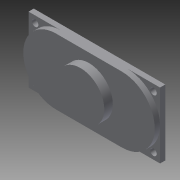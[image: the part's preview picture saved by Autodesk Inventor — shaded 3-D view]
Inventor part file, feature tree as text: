
AUTODESK INVENTOR PART (.ipt)
format: ipt  version: 2016 (Build 200138000, 138)  size: 116,736 bytes
history: native  units: mm
features: sketch x4, extrude x3, hole x1
ambient origin geometry x8: Origin, YZ Plane, XZ Plane, XY Plane, X Axis, Y Axis, Z Axis, Center Point
bodies: Solid1 (feature_tree)
feature tree (8):
  extrude  "Extrusion1"  Depth=20.0mm
  extrude  "Extrusion2"  Depth=20.0mm
  extrude  "Extrusion3"  Depth=10.0mm
  hole  "Hole1"  [1 undecoded]
  sketch  "Sketch1"  dims[d0=40.0mm d1=20.0mm]
  sketch  "Sketch2"  dims[d2=10.0mm d3=20.0mm]
  sketch  "Sketch3"  dims[d4=1.6mm d5=0.0mm d6=10.0mm]
  sketch  "Sketch4"  dims[d7=1.6mm d8=0.0mm d9=14.5mm d10=2.6mm d11=0.0mm d12=36.0mm d13=16.0mm d14=2.0mm d15=6.0mm d16=4.0mm d17=2.0mm d18=90.0deg d19=8.0mm d20=20.594885mm]
note: 1 required parameter value undecoded (feature->parameter linkage not recoverable at this tier; creation-order binding heuristic only, values carry confidence <= 0.55)
